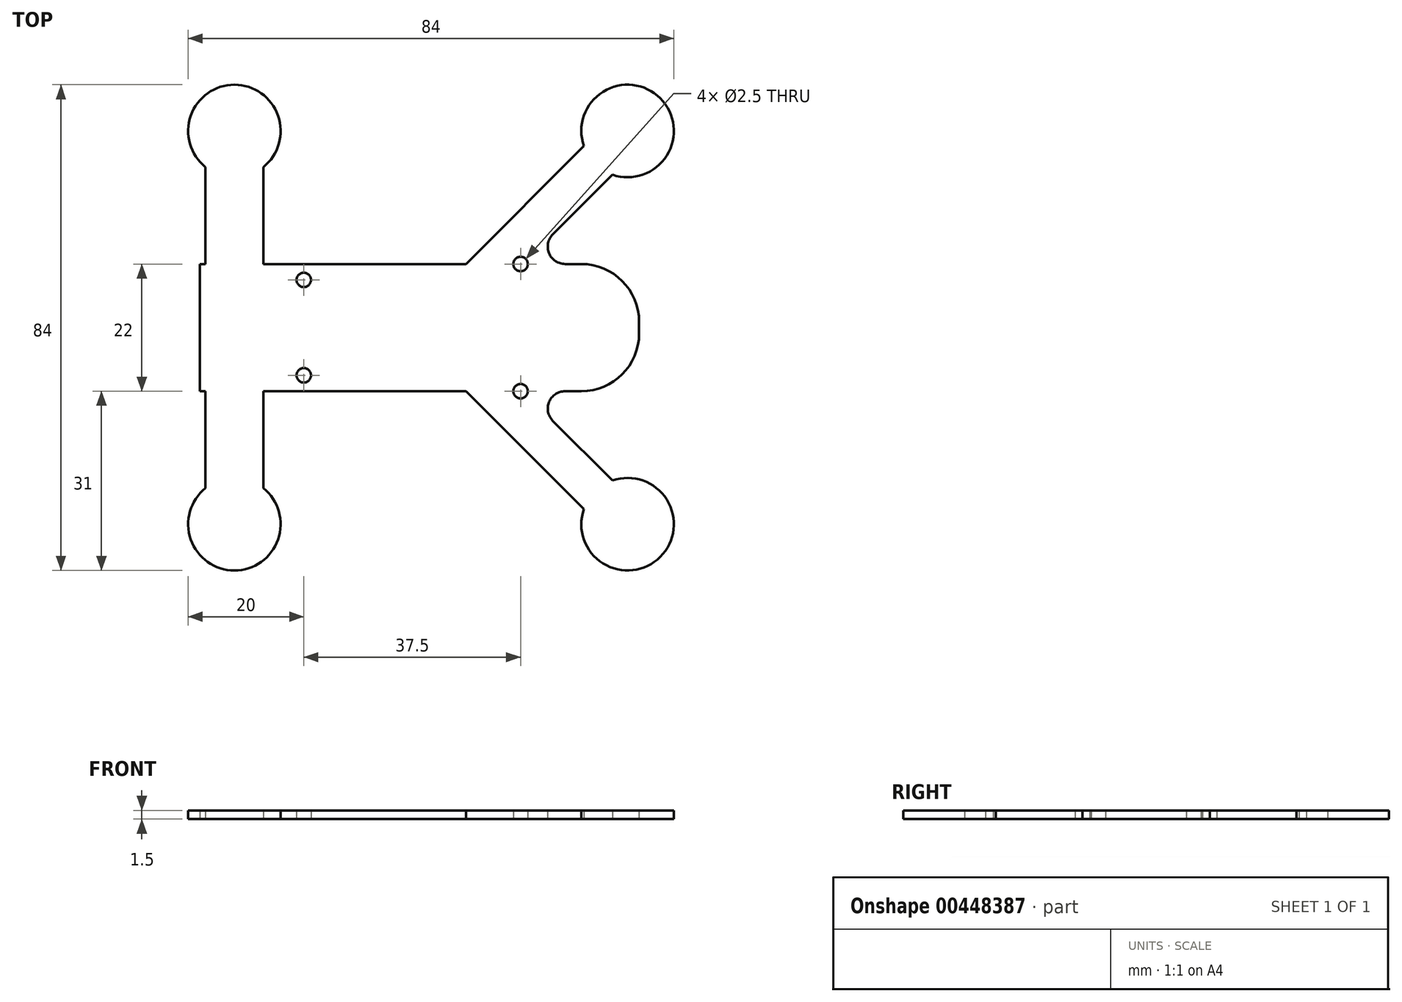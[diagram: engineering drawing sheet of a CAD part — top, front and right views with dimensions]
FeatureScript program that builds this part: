
annotation { "Feature Type Name" : "Feature", "Feature Type Description" : "" }
export const myFeature = defineFeature(function(context is Context, id is Id, definition is map)
    precondition{}
    {
        {
            var Q0;
            Q0=qCreatedBy(makeId("Top.planeOp"),FACE);
            var sketch = newSketch(context, id + "F0", { "sketchPlane" : qUnion([Q0])});
            skArc(sketch, "E0", {"start": v(-7, 27.76) * mm, "mid": v(-12, 42) * mm, "end": v(-17, 27.76) * mm});
            skArc(sketch, "E1", {"start": v(-17, -27.76) * mm, "mid": v(-12, -42) * mm, "end": v(-7, -27.76) * mm});
            skArc(sketch, "E2", {"start": v(48.44, -31.39) * mm, "mid": v(61.66, -39.66) * mm, "end": v(53.39, -26.44) * mm});
            skArc(sketch, "E3", {"start": v(53.39, 26.44) * mm, "mid": v(61.66, 39.66) * mm, "end": v(48.44, 31.39) * mm});
            skLineSegment(sketch, "E4.left", {"start": v(-17, 27.76) * mm, "end": v(-17, 11) * mm});
            skLineSegment(sketch, "E4.right", {"start": v(-7, 27.76) * mm, "end": v(-7, 11) * mm});
            skLineSegment(sketch, "E5", {"start": v(48.44, 31.39) * mm, "end": v(28.05, 11) * mm});
            skLineSegment(sketch, "E6", {"start": v(53.39, 26.44) * mm, "end": v(43.07, 16.12) * mm});
            skLineSegment(sketch, "E7.MirrorCS", {"start": v(53.39, -26.44) * mm, "end": v(43.07, -16.12) * mm});
            skLineSegment(sketch, "E8.MirrorCS", {"start": v(48.44, -31.39) * mm, "end": v(28.05, -11) * mm});
            skLineSegment(sketch, "E9.bottom", {"start": v(-18, 11) * mm, "end": v(-17, 11) * mm});
            skLineSegment(sketch, "E9.top", {"start": v(-18, -11) * mm, "end": v(-17, -11) * mm});
            skLineSegment(sketch, "E9.left", {"start": v(-18, 11) * mm, "end": v(-18, -11) * mm});
            skLineSegment(sketch, "E9.right", {"start": v(58, 1) * mm, "end": v(58, -1) * mm});
            skLineSegment(sketch, "E10.trimOffspring", {"start": v(-17, -11) * mm, "end": v(-17, -27.76) * mm});
            skLineSegment(sketch, "E11.trimOffspring", {"start": v(-7, 11) * mm, "end": v(28.05, 11) * mm});
            skLineSegment(sketch, "E12.trimOffspring", {"start": v(-7, -11) * mm, "end": v(28.05, -11) * mm});
            skLineSegment(sketch, "E13.trimOffspring", {"start": v(-7, -11) * mm, "end": v(-7, -27.76) * mm});
            skPoint(sketch, "E14.orphan", {"position": v(24.25, -7.2) * mm});
            skLineSegment(sketch, "E15.trimOffspring", {"start": v(45.2, -11) * mm, "end": v(48, -11) * mm});
            skPoint(sketch, "E16.orphan", {"position": v(24.25, 7.2) * mm});
            skPoint(sketch, "E17.orphan", {"position": v(37.6, -10.65) * mm});
            skPoint(sketch, "E18.orphan", {"position": v(37.6, 10.65) * mm});
            skLineSegment(sketch, "E19.trimOffspring", {"start": v(45.2, 11) * mm, "end": v(48, 11) * mm});
            skPoint(sketch, "E20.visualSharp", {"position": v(58, 11) * mm});
            skArc(sketch, "E20.filletArc", {"start": v(58, 1) * mm, "mid": v(55.07, 8.07) * mm, "end": v(48, 11) * mm});
            skPoint(sketch, "E21.visualSharp", {"position": v(58, -11) * mm});
            skArc(sketch, "E21.filletArc", {"start": v(48, -11) * mm, "mid": v(55.07, -8.07) * mm, "end": v(58, -1) * mm});
            skPoint(sketch, "E22.visualSharp", {"position": v(37.95, 11) * mm});
            skArc(sketch, "E22.filletArc", {"start": v(43.07, 16.12) * mm, "mid": v(42.42, 12.85) * mm, "end": v(45.2, 11) * mm});
            skPoint(sketch, "E23.visualSharp", {"position": v(37.95, -11) * mm});
            skArc(sketch, "E23.filletArc", {"start": v(45.2, -11) * mm, "mid": v(42.42, -12.85) * mm, "end": v(43.07, -16.12) * mm});
            skSolve(sketch);
        }
        {
            var Q0;
            Q0 = qSketchRegion(id + "F0", true);
            extrude(context, id + "F1", {"entities" : qUnion([Q0]), "depth" : 1.5 * mm});
        }
        {
            var Q0;
            Q0=qCreatedBy(makeId("Top.planeOp"),FACE);
            var sketch = newSketch(context, id + "F2", { "sketchPlane" : qUnion([Q0])});
            skCircle(sketch, "E24", {"center": v(0, 8.25) * mm, "radius": 1.25 * mm});
            skCircle(sketch, "E25", {"center": v(0, -8.25) * mm, "radius": 1.25 * mm});
            skCircle(sketch, "E26", {"center": v(37.5, 11) * mm, "radius": 1.25 * mm});
            skCircle(sketch, "E27", {"center": v(37.5, -11) * mm, "radius": 1.25 * mm});
            skSolve(sketch);
        }
        {
            var Q0;
            Q0=makeQuery(id+"F2.imprint","IMPRINT",FACE,{"disambiguationData":[TD([[makeQuery(id+"F2.imprint","IMPRINT",EDGE,{"derivedFrom":sQuery(id+"F2.wireOp",EDGE,"E25")}),1.0]])]});
            var Q1;
            Q1=makeQuery(id+"F2.imprint","IMPRINT",FACE,{"disambiguationData":[TD([[makeQuery(id+"F2.imprint","IMPRINT",EDGE,{"derivedFrom":sQuery(id+"F2.wireOp",EDGE,"E24")}),1.0]])]});
            var Q2;
            Q2=makeQuery(id+"F2.imprint","IMPRINT",FACE,{"disambiguationData":[TD([[makeQuery(id+"F2.imprint","IMPRINT",EDGE,{"derivedFrom":sQuery(id+"F2.wireOp",EDGE,"E27")}),1.0]])]});
            var Q3;
            Q3=makeQuery(id+"F2.imprint","IMPRINT",FACE,{"disambiguationData":[TD([[makeQuery(id+"F2.imprint","IMPRINT",EDGE,{"derivedFrom":sQuery(id+"F2.wireOp",EDGE,"E26")}),1.0]])]});
            extrude(context, id + "F3", {"entities" : qUnion([Q0, Q1, Q2, Q3]), "operationType" : NewBodyOperationType.REMOVE, "depth" : 25 * mm});
        }
    });
